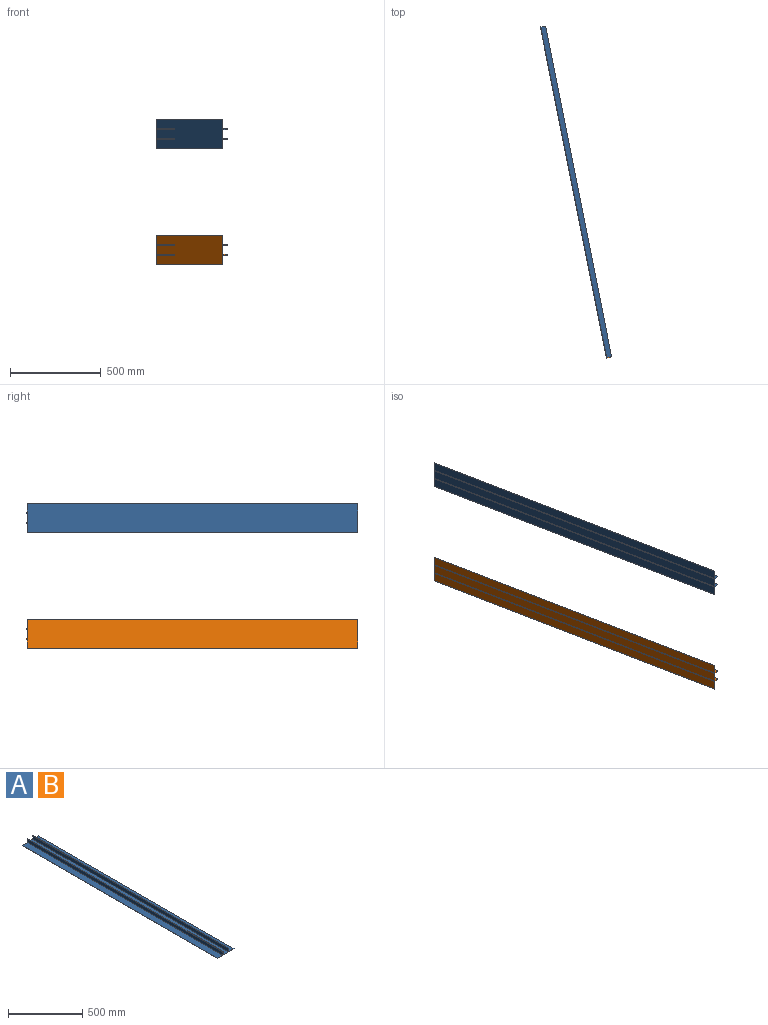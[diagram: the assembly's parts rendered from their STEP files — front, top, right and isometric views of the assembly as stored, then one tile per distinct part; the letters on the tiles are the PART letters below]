
ASSEMBLY  parts=2 mates=3
PART A: 14 faces, bbox 158x1860x30 mm
  f0: plane 1860x4mm, normal (0,0,1), area 7440mm2, adj f1,f11,f12,f13
  f1: plane 1860x28mm, normal (-1,0,0), area 52080mm2, adj f0,f2,f12,f13
  f2: plane 1860x50mm, normal (0,0,1), area 93000mm2, adj f1,f3,f12,f13
  f3: plane 1860x28mm, normal (1,0,0), area 52080mm2, adj f2,f4,f12,f13
  f4: plane 1860x4mm, normal (0,0,1), area 7440mm2, adj f3,f5,f12,f13
  f5: plane 1860x28mm, normal (-1,0,0), area 52080mm2, adj f4,f6,f12,f13
  f6: plane 1860x50mm, normal (0,0,1), area 93000mm2, adj f5,f7,f12,f13
  f7: plane 1860x2mm, normal (-1,0,0), area 3720mm2, adj f6,f8,f12,f13
  f8: plane 1860x158mm, normal (0,0,-1), area 293880mm2, adj f7,f9,f12,f13
  f9: plane 1860x2mm, normal (1,0,0), area 3720mm2, adj f8,f10,f12,f13
  f10: plane 1860x50mm, normal (0,0,1), area 93000mm2, adj f9,f11,f12,f13
  f11: plane 1860x28mm, normal (1,0,0), area 52080mm2, adj f0,f10,f12,f13
  f12: plane 158x30mm, normal (0,-1,0), area 540mm2, adj f0,f1,f2,f3,f4,f5,f6,f7
  f13: plane 158x30mm, normal (0,1,0), area 540mm2, adj f0,f1,f2,f3,f4,f5,f6,f7
PART B: same geometry as A
PLACE A rot(axis=(-0.1,0.99,0.1),90.6deg) t=(630.56,-804.36,1535.83)mm
PLACE B rot(axis=(-0.1,0.99,0.1),90.6deg) t=(630.56,-804.36,897.83)mm
MATE planar A.f12 <-> B.f12  axis (0.2,-0.98,0) through (1000.87,-2627.14,1456.83)mm
MATE parallel A.f7 <-> B.f7  axis (0,0,1) through (813.16,-1716.26,1535.83)mm
MATE planar A.f8 <-> B.f8  axis (-0.98,-0.2,0) through (812.18,-1716.46,1456.83)mm
